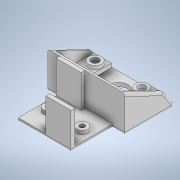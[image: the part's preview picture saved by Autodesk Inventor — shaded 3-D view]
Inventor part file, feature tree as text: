
AUTODESK INVENTOR PART (.ipt)
format: ipt  version: 2020 (Build 240168000, 168)  size: 302,080 bytes
history: native  units: in
note: dims shown in document units (in); Inventor stores cm internally (conversion verified against a paired STEP export)
features: sketch x15, extrude x14, fillet x1
ambient origin geometry x8: Origin, YZ Plane, XZ Plane, XY Plane, X Axis, Y Axis, Z Axis, Center Point
bodies: Solid1 (feature_tree)
feature tree (30):
  extrude  "Extrusion1"  Depth=1.2756in
  extrude  "Extrusion3"  Depth=0.1181in
  extrude  "Extrusion4"  Depth=1.0in TaperAngle=0.0deg
  extrude  "Extrusion5"  Depth=0.1181in TaperAngle=0.0deg
  extrude  "Extrusion6"  Depth=0.1181in TaperAngle=0.0deg
  extrude  "Extrusion7"  Depth=0.3346in
  extrude  "Extrusion8"  Depth=0.1181in
  extrude  "Extrusion9"  Depth=0.2362in TaperAngle=0.0deg
  extrude  "Extrusion10"  Depth=0.2362in
  extrude  "Extrusion11"  Depth=2.3622in
  extrude  "Extrusion12"  Depth=1.5748in TaperAngle=0.0deg
  extrude  "Extrusion13"  Depth=0.1181in
  extrude  "Extrusion14"  Depth=1.0in TaperAngle=0.0deg
  sketch  "Sketch15"  dims[d41=0.5906in d42=0.1181in d43=0.5512in d44=0.0in]
  extrude  "Extrusion15"  Depth=0.1181in
  fillet  "Fillet1"  Radius=0.5512in
  sketch  "Sketch1"  dims[d0=1.6142in d1=1.2756in]
  sketch  "Sketch3"  dims[d2=0.1181in d3=0.0in d8=0.1181in]
  sketch  "Sketch4"  dims[d9=0.1181in d10=1.0in d11=0.0in]
  sketch  "Sketch5"  dims[d12=0.8465in d13=0.1181in d14=0.0in]
  sketch  "Sketch6"  dims[d15=0.8465in d16=0.1181in d17=0.0in]
  sketch  "Sketch7"  dims[d20=0.3346in d21=0.3346in]
  sketch  "Sketch8"  dims[d22=0.1181in d23=0.0in d24=0.1575in]
  sketch  "Sketch9"  dims[d25=0.1575in d26=0.2362in d27=0.0in]
  sketch  "Sketch10"  dims[d28=0.2362in d29=0.2362in]
  sketch  "Sketch11"  dims[d30=0.1181in d31=0.0in d32=2.3622in]
  sketch  "Sketch12"  dims[d33=0.1181in d34=1.5748in d35=0.0in]
  sketch  "Sketch13"  dims[d36=0.1181in d37=0.1181in]
  sketch  "Sketch14"  dims[d38=0.1181in d39=1.0in d40=0.0in]
  sketch  "Sketch16"  dims[d45=0.5512in d46=0.0in d47=0.5906in d48=0.1575in d49=0.1575in d50=0.5512in d51=0.0in d52=0.2362in d53=0.3937in d54=0.2362in d55=0.3937in d56=0.1181in d57=0.0in d58=2.3622in d59=0.0in d60=0.0787in d61=0.0344in]
